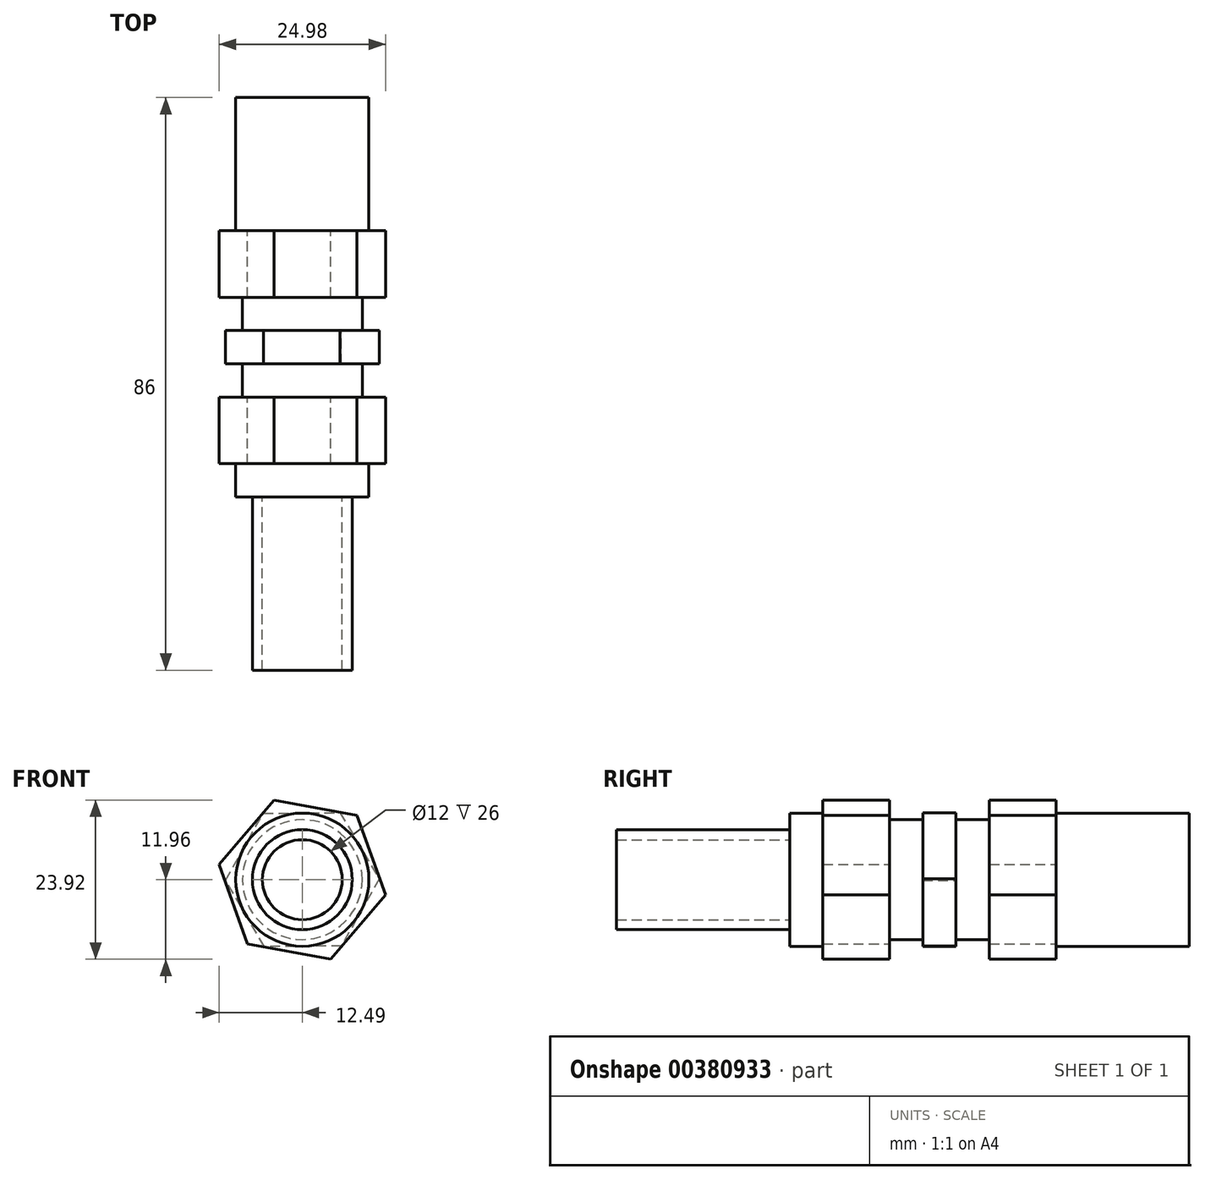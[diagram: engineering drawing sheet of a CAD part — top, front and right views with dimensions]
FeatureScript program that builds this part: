
annotation { "Feature Type Name" : "Feature", "Feature Type Description" : "" }
export const myFeature = defineFeature(function(context is Context, id is Id, definition is map)
    precondition{}
    {
        {
            var Q0;
            Q0=qCreatedBy(makeId("Front.planeOp"),FACE);
            var sketch = newSketch(context, id + "F0", { "sketchPlane" : qUnion([Q0])});
            skCircle(sketch, "E0", {"center": v(0, 0) * mm, "radius": 10 * mm});
            skSolve(sketch);
        }
        {
            var Q0;
            Q0=makeQuery(id+"F0.imprint","IMPRINT",FACE,{"disambiguationData":[TD([[makeQuery(id+"F0.imprint","IMPRINT",EDGE,{"derivedFrom":sQuery(id+"F0.wireOp",EDGE,"E0")}),1.0]])]});
            extrude(context, id + "F1", {"entities" : qUnion([Q0]), "endBound" : BoundingType.SYMMETRIC, "depth" : 20 * mm});
        }
        {
            var Q0;
            Q0=makeQuery(id+"F1.opExtrude","CAP_FACE",FACE,{"disambiguationData":[OSD([sQuery(id+"F0.wireOp",EDGE,"E0")])],"isStart":false});
            var sketch = newSketch(context, id + "F2", { "sketchPlane" : qUnion([Q0])});
            skCircle(sketch, "E1.cCircle", {"center": v(0, 0) * mm, "radius": 11 * mm, "construction": true});
            skLineSegment(sketch, "E1.0", {"start": v(12.5, -2.29) * mm, "end": v(4.26, -11.96) * mm});
            skLineSegment(sketch, "E1.1", {"start": v(4.26, -11.96) * mm, "end": v(-8.23, -9.68) * mm});
            skLineSegment(sketch, "E1.2", {"start": v(-8.23, -9.68) * mm, "end": v(-12.5, 2.29) * mm});
            skLineSegment(sketch, "E1.3", {"start": v(-12.5, 2.29) * mm, "end": v(-4.26, 11.96) * mm});
            skLineSegment(sketch, "E1.4", {"start": v(-4.26, 11.96) * mm, "end": v(8.23, 9.68) * mm});
            skLineSegment(sketch, "E1.5", {"start": v(8.23, 9.68) * mm, "end": v(12.5, -2.29) * mm});
            skPoint(sketch, "E1.0.midPoint", {"position": v(8.38, -7.13) * mm});
            skSolve(sketch);
        }
        {
            var Q0;
            Q0 = qSketchRegion(id + "F2", true);
            extrude(context, id + "F3", {"entities" : qUnion([Q0]), "operationType" : NewBodyOperationType.ADD, "depth" : 10 * mm});
        }
        {
            var Q0;
            Q0=makeQuery(id+"F3.opExtrude","CAP_FACE",FACE,{"disambiguationData":[OSD([sQuery(id+"F2.wireOp",EDGE,"E1.0"),sQuery(id+"F2.wireOp",EDGE,"E1.1"),sQuery(id+"F2.wireOp",EDGE,"E1.2"),sQuery(id+"F2.wireOp",EDGE,"E1.3"),sQuery(id+"F2.wireOp",EDGE,"E1.4"),sQuery(id+"F2.wireOp",EDGE,"E1.5")])],"isStart":false});
            var sketch = newSketch(context, id + "F4", { "sketchPlane" : qUnion([Q0])});
            skCircle(sketch, "E2", {"center": v(0, 0) * mm, "radius": 9 * mm});
            skSolve(sketch);
        }
        {
            var Q0;
            Q0 = qSketchRegion(id + "F4", true);
            extrude(context, id + "F5", {"entities" : qUnion([Q0]), "operationType" : NewBodyOperationType.ADD, "depth" : 5 * mm});
        }
        {
            var Q0;
            Q0=makeQuery(id+"F5.opExtrude","CAP_FACE",FACE,{"disambiguationData":[OSD([sQuery(id+"F4.wireOp",EDGE,"E2")])],"isStart":false});
            var sketch = newSketch(context, id + "F6", { "sketchPlane" : qUnion([Q0])});
            skCircle(sketch, "E3.cCircle", {"center": v(0, 0) * mm, "radius": 10 * mm, "construction": true});
            skLineSegment(sketch, "E3.0", {"start": v(11.55, 0.1) * mm, "end": v(5.86, -9.95) * mm});
            skLineSegment(sketch, "E3.1", {"start": v(5.86, -9.95) * mm, "end": v(-5.69, -10.05) * mm});
            skLineSegment(sketch, "E3.2", {"start": v(-5.69, -10.05) * mm, "end": v(-11.55, -0.1) * mm});
            skLineSegment(sketch, "E3.3", {"start": v(-11.55, -0.1) * mm, "end": v(-5.86, 9.95) * mm});
            skLineSegment(sketch, "E3.4", {"start": v(-5.86, 9.95) * mm, "end": v(5.69, 10.05) * mm});
            skLineSegment(sketch, "E3.5", {"start": v(5.69, 10.05) * mm, "end": v(11.55, 0.1) * mm});
            skPoint(sketch, "E3.0.midPoint", {"position": v(8.7, -4.93) * mm});
            skSolve(sketch);
        }
        {
            var Q0;
            Q0 = qSketchRegion(id + "F6", true);
            extrude(context, id + "F7", {"entities" : qUnion([Q0]), "operationType" : NewBodyOperationType.ADD, "depth" : 5 * mm});
        }
        {
            var Q0;
            Q0=makeQuery(id+"F7.opExtrude","CAP_FACE",FACE,{"disambiguationData":[OSD([sQuery(id+"F6.wireOp",EDGE,"E3.0"),sQuery(id+"F6.wireOp",EDGE,"E3.1"),sQuery(id+"F6.wireOp",EDGE,"E3.2"),sQuery(id+"F6.wireOp",EDGE,"E3.3"),sQuery(id+"F6.wireOp",EDGE,"E3.4"),sQuery(id+"F6.wireOp",EDGE,"E3.5")])],"isStart":false});
            var sketch = newSketch(context, id + "F8", { "sketchPlane" : qUnion([Q0])});
            skCircle(sketch, "E4", {"center": v(0, 0) * mm, "radius": 9 * mm});
            skSolve(sketch);
        }
        {
            var Q0;
            Q0 = qSketchRegion(id + "F8", true);
            extrude(context, id + "F9", {"entities" : qUnion([Q0]), "operationType" : NewBodyOperationType.ADD, "depth" : 5 * mm});
        }
        {
            var Q0;
            Q0=makeQuery(id+"F9.opExtrude","CAP_FACE",FACE,{"disambiguationData":[OSD([sQuery(id+"F8.wireOp",EDGE,"E4")])],"isStart":false});
            var sketch = newSketch(context, id + "F10", { "sketchPlane" : qUnion([Q0])});
            skLineSegment(sketch, "E5.0", {"start": v(-4.26, 11.96) * mm, "end": v(8.23, 9.68) * mm});
            skLineSegment(sketch, "E6.0", {"start": v(8.23, 9.68) * mm, "end": v(12.5, -2.29) * mm});
            skPoint(sketch, "E7.0", {"position": v(4.26, -11.96) * mm});
            skLineSegment(sketch, "E8.0", {"start": v(12.5, -2.29) * mm, "end": v(4.26, -11.96) * mm});
            skLineSegment(sketch, "E9.0", {"start": v(4.26, -11.96) * mm, "end": v(-8.23, -9.68) * mm});
            skLineSegment(sketch, "E10.0", {"start": v(-8.23, -9.68) * mm, "end": v(-12.5, 2.29) * mm});
            skLineSegment(sketch, "E11.0", {"start": v(-12.5, 2.29) * mm, "end": v(-4.26, 11.96) * mm});
            skSolve(sketch);
        }
        {
            var Q0;
            Q0 = qSketchRegion(id + "F10", true);
            extrude(context, id + "F11", {"entities" : qUnion([Q0]), "operationType" : NewBodyOperationType.ADD, "depth" : 10 * mm});
        }
        {
            var Q0;
            Q0=makeQuery(id+"F11.opExtrude","CAP_FACE",FACE,{"disambiguationData":[OSD([sQuery(id+"F10.wireOp",EDGE,"E5.0"),sQuery(id+"F10.wireOp",EDGE,"E6.0"),sQuery(id+"F10.wireOp",EDGE,"E8.0"),sQuery(id+"F10.wireOp",EDGE,"E9.0"),sQuery(id+"F10.wireOp",EDGE,"E10.0"),sQuery(id+"F10.wireOp",EDGE,"E11.0")])],"isStart":false});
            var sketch = newSketch(context, id + "F12", { "sketchPlane" : qUnion([Q0])});
            skCircle(sketch, "E12", {"center": v(0, 0) * mm, "radius": 10 * mm});
            skSolve(sketch);
        }
        {
            var Q0;
            Q0 = qSketchRegion(id + "F12", true);
            extrude(context, id + "F13", {"entities" : qUnion([Q0]), "operationType" : NewBodyOperationType.ADD, "depth" : 5 * mm});
        }
        {
            var Q0;
            Q0=makeQuery(id+"F13.opExtrude","CAP_FACE",FACE,{"disambiguationData":[OSD([sQuery(id+"F12.wireOp",EDGE,"E12")])],"isStart":false});
            var sketch = newSketch(context, id + "F14", { "sketchPlane" : qUnion([Q0])});
            skCircle(sketch, "E13", {"center": v(0, 0) * mm, "radius": 7.5 * mm});
            skCircle(sketch, "E14", {"center": v(0, 0) * mm, "radius": 6 * mm});
            skSolve(sketch);
        }
        {
            var Q0;
            Q0=qCreatedBy(makeId("Front.planeOp"),FACE);
            cPlane(context, id + "F15", {"entities" : qUnion([Q0]), "cplaneType" : CPlaneType.OFFSET, "offset" : 76 * mm, "width" : 152.4 * mm, "height" : 152.4 * mm});
        }
        {
            var Q0;
            Q0 = qSketchRegion(id + "F14", true);
            var Q1;
            Q1=qCreatedBy(id+"F15.planeOp",FACE);
            extrude(context, id + "F16", {"entities" : qUnion([Q0]), "operationType" : NewBodyOperationType.ADD, "endBound" : BoundingType.UP_TO_SURFACE, "endBoundEntityFace" : qUnion([Q1]), "depth" : 25.4 * mm});
        }
    });
